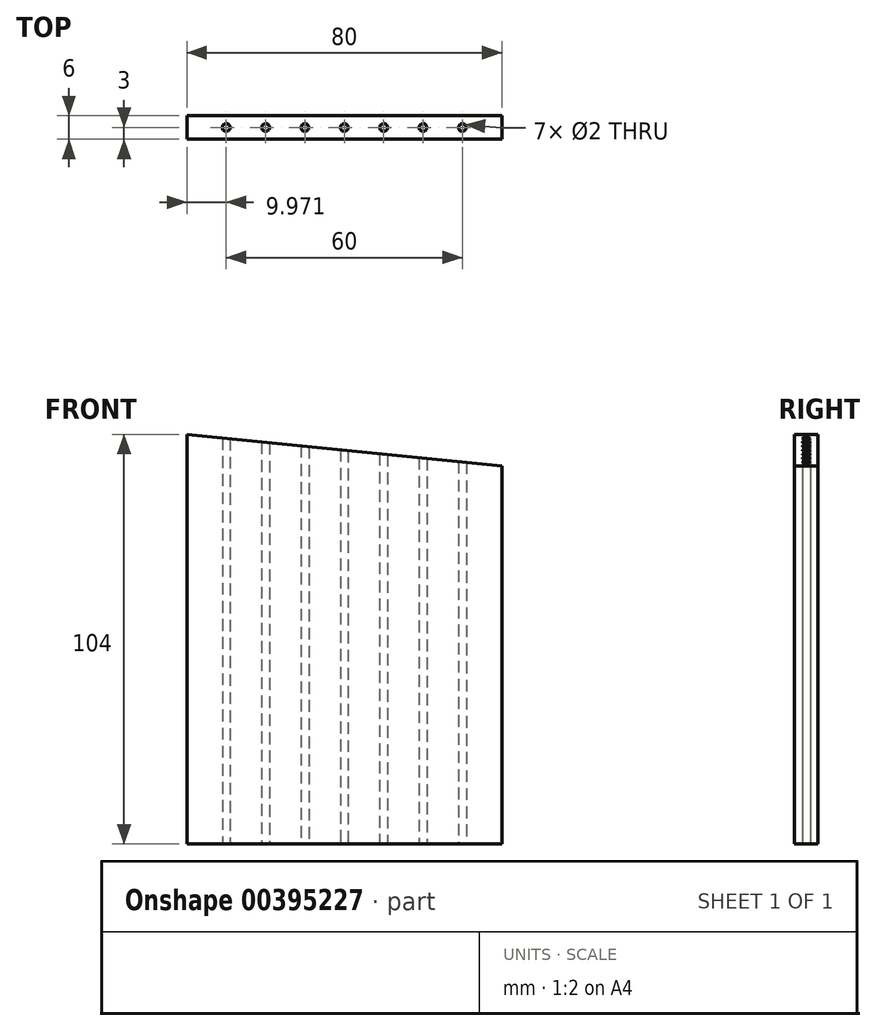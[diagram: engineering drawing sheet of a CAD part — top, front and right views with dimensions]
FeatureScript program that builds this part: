
annotation { "Feature Type Name" : "Feature", "Feature Type Description" : "" }
export const myFeature = defineFeature(function(context is Context, id is Id, definition is map)
    precondition{}
    {
        {
            var Q0;
            Q0=qCreatedBy(makeId("Front.planeOp"),FACE);
            var sketch = newSketch(context, id + "F0", { "sketchPlane" : qUnion([Q0])});
            skLineSegment(sketch, "E0", {"start": v(-31.12, 0) * mm, "end": v(48.88, 0) * mm});
            skLineSegment(sketch, "E1", {"start": v(48.88, 0) * mm, "end": v(48.88, 96) * mm});
            skLineSegment(sketch, "E2", {"start": v(-31.12, 0) * mm, "end": v(-31.12, 104) * mm});
            skLineSegment(sketch, "E3", {"start": v(-31.12, 104) * mm, "end": v(48.88, 96) * mm});
            skSolve(sketch);
        }
        {
            var Q0;
            Q0=makeQuery(id+"F0.imprint","IMPRINT",FACE,{"disambiguationData":[TD([[makeQuery(id+"F0.imprint","IMPRINT",EDGE,{"derivedFrom":sQuery(id+"F0.wireOp",EDGE,"E0")}),1.0]])]});
            extrude(context, id + "F1", {"entities" : qUnion([Q0]), "depth" : 6 * mm});
        }
        {
            var Q0;
            Q0=qCreatedBy(makeId("Top.planeOp"),FACE);
            var sketch = newSketch(context, id + "F2", { "sketchPlane" : qUnion([Q0])});
            skLineSegment(sketch, "E4", {"start": v(-31.15, -3) * mm, "end": v(48.85, -3) * mm, "construction": true});
            skCircle(sketch, "E5", {"center": v(-21.15, -3) * mm, "radius": 1 * mm});
            skCircle(sketch, "E6.1.0.0", {"center": v(-11.15, -3) * mm, "radius": 1 * mm});
            skCircle(sketch, "E6.2.0.0", {"center": v(-1.15, -3) * mm, "radius": 1 * mm});
            skCircle(sketch, "E6.3.0.0", {"center": v(8.85, -3) * mm, "radius": 1 * mm});
            skCircle(sketch, "E6.4.0.0", {"center": v(18.85, -3) * mm, "radius": 1 * mm});
            skCircle(sketch, "E6.5.0.0", {"center": v(28.85, -3) * mm, "radius": 1 * mm});
            skCircle(sketch, "E6.6.0.0", {"center": v(38.85, -3) * mm, "radius": 1 * mm});
            skLineSegment(sketch, "E6.direction1", {"start": v(-21.15, -3) * mm, "end": v(-11.15, -3) * mm, "construction": true});
            skSolve(sketch);
        }
        {
            var Q0;
            Q0 = qSketchRegion(id + "F2", true);
            extrude(context, id + "F3", {"entities" : qUnion([Q0]), "operationType" : NewBodyOperationType.REMOVE, "depth" : 110 * mm});
        }
    });
